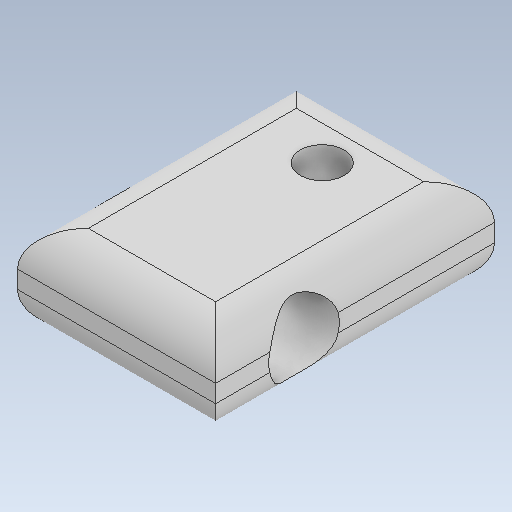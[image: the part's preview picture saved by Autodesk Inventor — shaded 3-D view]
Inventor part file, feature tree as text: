
AUTODESK INVENTOR PART (.ipt)
format: ipt  version: 2021 (Build 250183000, 183)  size: 143,360 bytes
history: native  units: mm
features: extrude x3, sketch x3, fillet x1
ambient origin geometry x8: Origin, YZ Plane, XZ Plane, XY Plane, X Axis, Y Axis, Z Axis, Center Point
bodies: Solid1 (feature_tree)
feature tree (7):
  extrude  "Extrusion1"  TaperAngle=0.0deg  [1 undecoded]
  extrude  "Extrusion2"  Depth=2.0mm
  fillet  "Fillet1"  Radius=2.0mm
  extrude  "Extrusion3"  TaperAngle=0.0deg  [1 undecoded]
  sketch  "Sketch1"  dims[d0=5.0mm d1=0.0mm d4=0.0mm d5=0.0mm]
  sketch  "Sketch2"  dims[d6=4.0mm d7=5.0mm d8=2.0mm]
  sketch  "Sketch3"  dims[d9=2.5mm d10=0.0mm d11=0.0mm]
note: 2 required parameter values undecoded (feature->parameter linkage not recoverable at this tier; creation-order binding heuristic only, values carry confidence <= 0.55)
